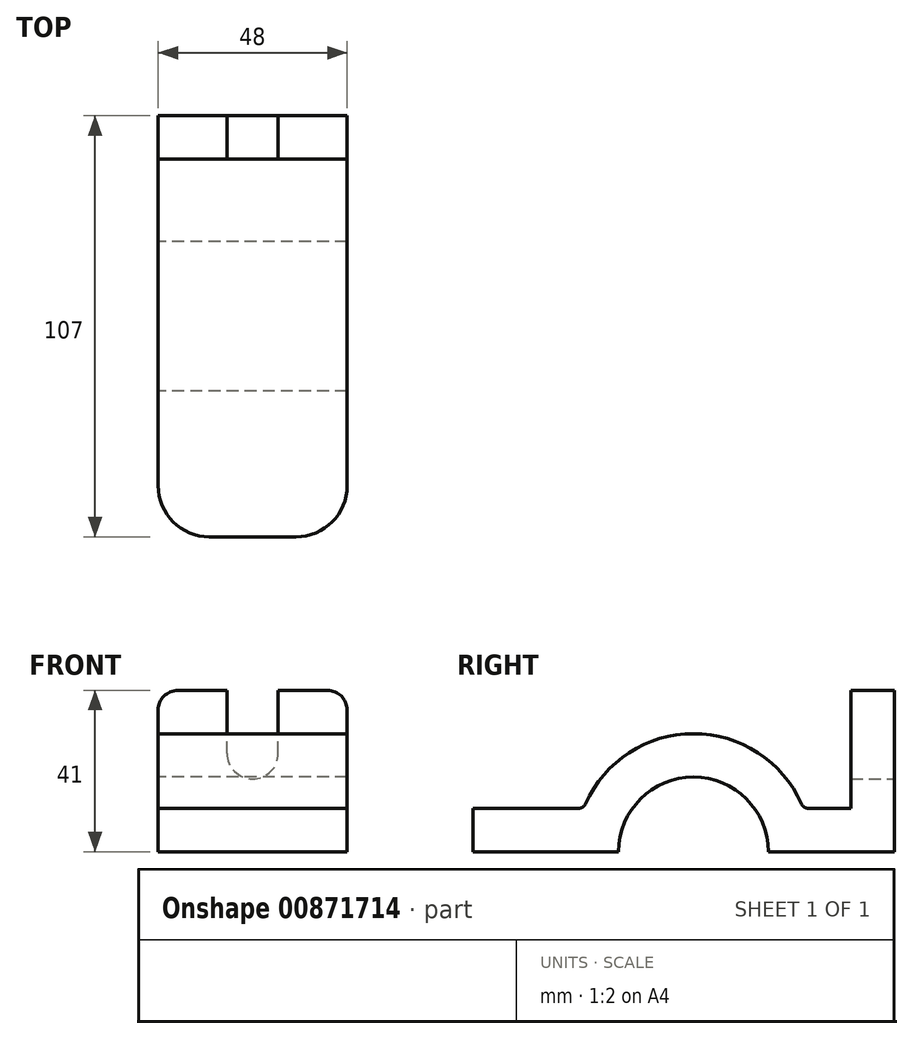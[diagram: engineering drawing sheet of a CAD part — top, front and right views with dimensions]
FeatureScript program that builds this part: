
annotation { "Feature Type Name" : "Feature", "Feature Type Description" : "" }
export const myFeature = defineFeature(function(context is Context, id is Id, definition is map)
    precondition{}
    {
        {
            var Q0;
            Q0=qCreatedBy(makeId("Right.planeOp"),FACE);
            var sketch = newSketch(context, id + "F0", { "sketchPlane" : qUnion([Q0])});
            skCircle(sketch, "E0", {"center": v(0, 0) * mm, "radius": 19 * mm});
            skCircle(sketch, "E1", {"center": v(0, 0) * mm, "radius": 30 * mm});
            skLineSegment(sketch, "E2.bottom", {"start": v(-56, 0) * mm, "end": v(51, 0) * mm});
            skLineSegment(sketch, "E2.top", {"start": v(-56, 11) * mm, "end": v(51, 11) * mm});
            skLineSegment(sketch, "E2.left", {"start": v(-56, 0) * mm, "end": v(-56, 11) * mm});
            skLineSegment(sketch, "E2.right", {"start": v(51, 0) * mm, "end": v(51, 11) * mm});
            skLineSegment(sketch, "E3.bottom", {"start": v(51, 11) * mm, "end": v(40, 11) * mm});
            skLineSegment(sketch, "E3.top", {"start": v(51, 41) * mm, "end": v(40, 41) * mm});
            skLineSegment(sketch, "E3.left", {"start": v(51, 11) * mm, "end": v(51, 41) * mm});
            skLineSegment(sketch, "E3.right", {"start": v(40, 11) * mm, "end": v(40, 41) * mm});
            skSolve(sketch);
        }
        {
            var Q0;
            {var subQ5=sQuery(id+"F0.wireOp",EDGE,"E2.left");Q0=makeQuery(id+"F0.imprint","IMPRINT",FACE,{"disambiguationData":[TD([[makeQuery(id+"F0.imprint","IMPRINT",EDGE,{"derivedFrom":subQ5}),-1.0]])]});}
            var Q1;
            {var subQ0=sQuery(id+"F0.wireOp",EDGE,"E2.bottom");var subQ1=sQuery(id+"F0.wireOp",EDGE,"E0");var subQ2=makeQuery(id+"F0.imprint","INTERSECT",VERTEX,{"disambiguationData":[OD(0.0)],"derivedFrom":[subQ1,subQ0]});Q1=makeQuery(id+"F0.imprint","IMPRINT",FACE,{"disambiguationData":[TD([[makeQuery(id+"F0.imprint","IMPRINT",EDGE,{"disambiguationData":[TD([[subQ2,1.0]])],"derivedFrom":subQ1}),-1.0]])]});}
            var Q2;
            {var subQ0=sQuery(id+"F0.wireOp",EDGE,"E2.top");var subQ1=sQuery(id+"F0.wireOp",EDGE,"E0");var subQ2=makeQuery(id+"F0.imprint","INTERSECT",VERTEX,{"disambiguationData":[OD(0.0)],"derivedFrom":[subQ1,subQ0]});Q2=makeQuery(id+"F0.imprint","IMPRINT",FACE,{"disambiguationData":[TD([[makeQuery(id+"F0.imprint","IMPRINT",EDGE,{"disambiguationData":[TD([[subQ2,1.0]])],"derivedFrom":subQ1}),-1.0]])]});}
            var Q3;
            {var subQ0=sQuery(id+"F0.wireOp",EDGE,"E2.top");var subQ1=sQuery(id+"F0.wireOp",EDGE,"E0");var subQ2=makeQuery(id+"F0.imprint","INTERSECT",VERTEX,{"disambiguationData":[OD(1.0)],"derivedFrom":[subQ1,subQ0]});Q3=makeQuery(id+"F0.imprint","IMPRINT",FACE,{"disambiguationData":[TD([[makeQuery(id+"F0.imprint","IMPRINT",EDGE,{"disambiguationData":[TD([[subQ2,1.0]])],"derivedFrom":subQ1}),-1.0]])]});}
            var Q4;
            {var subQ0=sQuery(id+"F0.wireOp",EDGE,"E2.right");Q4=makeQuery(id+"F0.imprint","IMPRINT",FACE,{"disambiguationData":[TD([[makeQuery(id+"F0.imprint","IMPRINT",EDGE,{"derivedFrom":subQ0}),1.0]])]});}
            var Q5;
            Q5=makeQuery(id+"F0.imprint","IMPRINT",FACE,{"disambiguationData":[TD([[makeQuery(id+"F0.imprint","IMPRINT",EDGE,{"derivedFrom":sQuery(id+"F0.wireOp",EDGE,"E3.top")}),1.0]])]});
            extrude(context, id + "F1", {"entities" : qUnion([Q0, Q1, Q2, Q3, Q4, Q5]), "endBound" : BoundingType.SYMMETRIC, "depth" : 48 * mm});
        }
        {
            var Q0;
            Q0=makeQuery(id+"F1.opExtrude","SWEPT_FACE",FACE,{"disambiguationData":[OSD([sQuery(id+"F0.wireOp",EDGE,"E2.right"),sQuery(id+"F0.wireOp",EDGE,"E3.left")])]});
            var sketch = newSketch(context, id + "F2", { "sketchPlane" : qUnion([Q0])});
            skLineSegment(sketch, "E4", {"start": v(0, 0) * mm, "end": v(0, 41) * mm, "construction": true});
            skCircle(sketch, "E5", {"center": v(0, 25) * mm, "radius": 6.5 * mm});
            skLineSegment(sketch, "E6", {"start": v(-6.5, 25) * mm, "end": v(-6.5, 41) * mm});
            skLineSegment(sketch, "E7", {"start": v(6.5, 25) * mm, "end": v(6.5, 41) * mm});
            skSolve(sketch);
        }
        {
            var Q0;
            {var subQ0=sQuery(id+"F2.wireOp",EDGE,"E5");var subQ2=makeQuery(id+"F2.imprint","INTERSECT",VERTEX,{"derivedFrom":[subQ0,sQuery(id+"F2.wireOp",EDGE,"E6")]});Q0=makeQuery(id+"F2.imprint","IMPRINT",FACE,{"disambiguationData":[TD([[makeQuery(id+"F2.imprint","IMPRINT",EDGE,{"disambiguationData":[TD([[subQ2,1.0]])],"derivedFrom":subQ0}),1.0]])]});}
            var Q1;
            {var subQ2=sQuery(id+"F2.wireOp",EDGE,"E6");Q1=makeQuery(id+"F2.imprint","IMPRINT",FACE,{"disambiguationData":[TD([[makeQuery(id+"F2.imprint","IMPRINT",EDGE,{"derivedFrom":subQ2}),-1.0]])]});}
            var Q2;
            Q2=makeQuery(id+"F1.opExtrude","SWEPT_FACE",FACE,{"disambiguationData":[OSD([sQuery(id+"F0.wireOp",EDGE,"E3.right")])]});
            extrude(context, id + "F3", {"entities" : qUnion([Q0, Q1]), "operationType" : NewBodyOperationType.REMOVE, "endBound" : BoundingType.UP_TO_SURFACE, "oppositeDirection" : true, "endBoundEntityFace" : qUnion([Q2]), "depth" : 25 * mm});
        }
        {
            var Q0;
            Q0=makeQuery(id+"F1.opExtrude","CAP_EDGE",EDGE,{"disambiguationData":[OSD([sQuery(id+"F0.wireOp",EDGE,"E2.left")])],"isStart":false});
            var Q1;
            Q1=makeQuery(id+"F1.opExtrude","CAP_EDGE",EDGE,{"disambiguationData":[OSD([sQuery(id+"F0.wireOp",EDGE,"E2.left")])],"isStart":true});
            fillet(context, id + "F5", {"entities" : qUnion([Q0, Q1]), "radius" : 13 * mm, "tangentPropagation" : true, "allowEdgeOverflow" : false});
        }
        {
            var Q0;
            Q0=makeQuery(id+"F1.opExtrude","CAP_EDGE",EDGE,{"disambiguationData":[OSD([sQuery(id+"F0.wireOp",EDGE,"E3.top")])],"isStart":false});
            var Q1;
            Q1=makeQuery(id+"F1.opExtrude","CAP_EDGE",EDGE,{"disambiguationData":[OSD([sQuery(id+"F0.wireOp",EDGE,"E3.top")])],"isStart":true});
            fillet(context, id + "F6", {"entities" : qUnion([Q0, Q1]), "radius" : 5 * mm, "tangentPropagation" : true, "allowEdgeOverflow" : false});
        }
        {
            var Q0;
            {var subQ0=sQuery(id+"F0.wireOp",EDGE,"E2.top");var subQ1=sQuery(id+"F0.wireOp",EDGE,"E1");Q0=makeQuery(id+"F1.opExtrude","SWEPT_EDGE",EDGE,{"disambiguationData":[OSD([subQ1,subQ0]),TDD([makeQuery(id+"F0.imprint","INTERSECT",VERTEX,{"disambiguationData":[OD(1.0)],"derivedFrom":[subQ1,subQ0]})])]});}
            var Q1;
            {var subQ0=sQuery(id+"F0.wireOp",EDGE,"E2.top");var subQ1=sQuery(id+"F0.wireOp",EDGE,"E1");Q1=makeQuery(id+"F1.opExtrude","SWEPT_EDGE",EDGE,{"disambiguationData":[OSD([subQ1,subQ0]),TDD([makeQuery(id+"F0.imprint","INTERSECT",VERTEX,{"disambiguationData":[OD(0.0)],"derivedFrom":[subQ1,subQ0]})])]});}
            fillet(context, id + "F7", {"entities" : qUnion([Q0, Q1]), "radius" : 2 * mm, "tangentPropagation" : true, "allowEdgeOverflow" : false});
        }
    });
